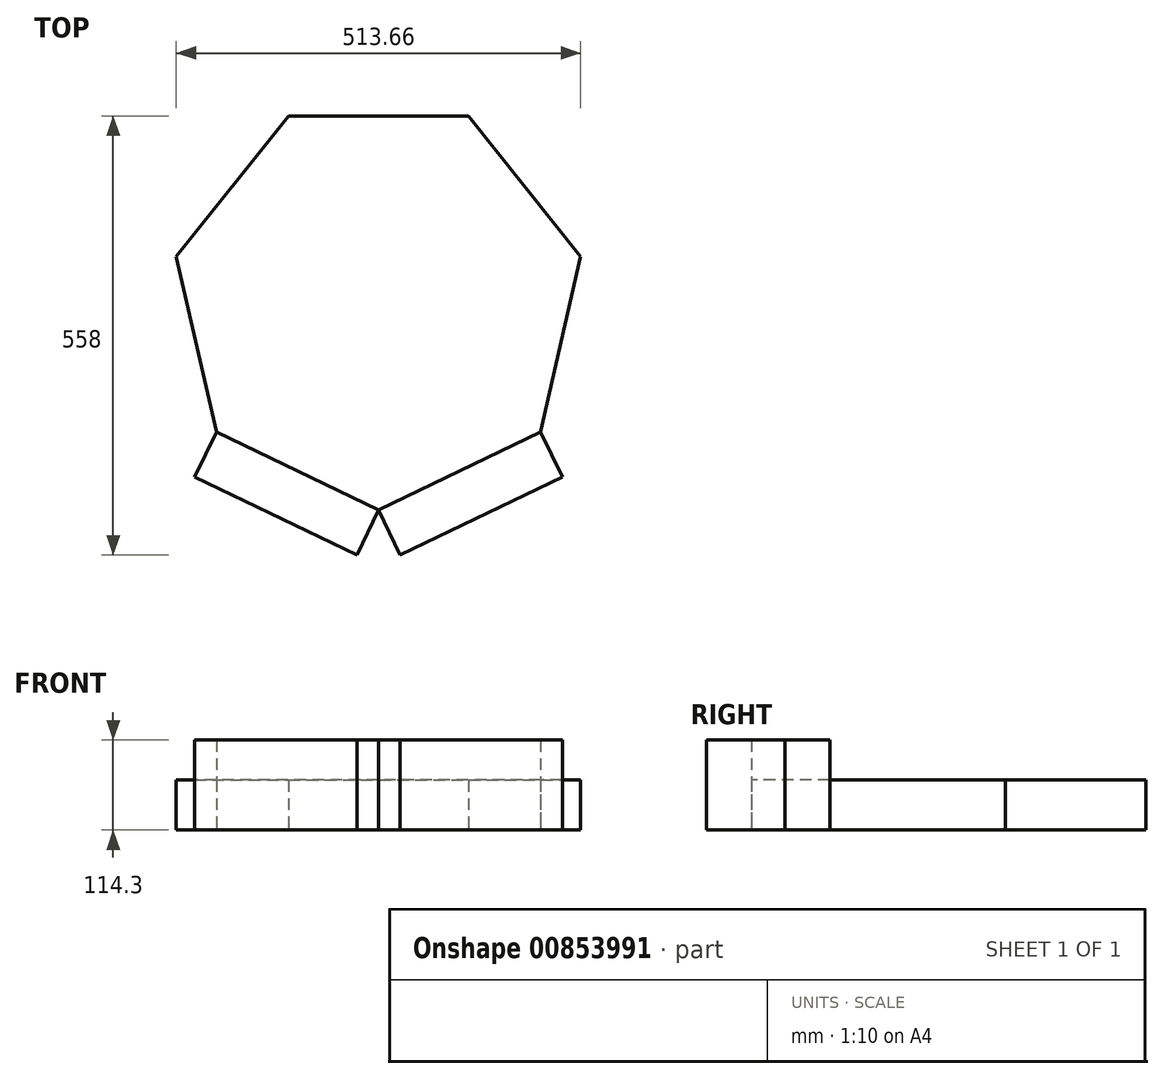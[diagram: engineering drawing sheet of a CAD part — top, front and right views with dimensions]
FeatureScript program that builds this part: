
annotation { "Feature Type Name" : "Feature", "Feature Type Description" : "" }
export const myFeature = defineFeature(function(context is Context, id is Id, definition is map)
    precondition{}
    {
        {
            var Q0;
            Q0=qCreatedBy(makeId("Top.planeOp"),FACE);
            var sketch = newSketch(context, id + "F0", { "sketchPlane" : qUnion([Q0])});
            skCircle(sketch, "E0.cCircle", {"center": v(0, 0) * mm, "radius": 237.35 * mm, "construction": true});
            skLineSegment(sketch, "E0.0", {"start": v(-114.3, 237.35) * mm, "end": v(114.3, 237.35) * mm});
            skLineSegment(sketch, "E0.1", {"start": v(114.3, 237.35) * mm, "end": v(256.83, 58.62) * mm});
            skLineSegment(sketch, "E0.2", {"start": v(256.83, 58.62) * mm, "end": v(205.96, -164.25) * mm});
            skLineSegment(sketch, "E0.3", {"start": v(205.96, -164.25) * mm, "end": v(0, -263.43) * mm});
            skLineSegment(sketch, "E0.4", {"start": v(0, -263.43) * mm, "end": v(-205.96, -164.25) * mm});
            skLineSegment(sketch, "E0.5", {"start": v(-205.96, -164.25) * mm, "end": v(-256.83, 58.62) * mm});
            skLineSegment(sketch, "E0.6", {"start": v(-256.83, 58.62) * mm, "end": v(-114.3, 237.35) * mm});
            skPoint(sketch, "E0.0.midPoint", {"position": v(0, 237.35) * mm});
            skSolve(sketch);
        }
        {
            var Q0;
            Q0 = qSketchRegion(id + "F0", true);
            extrude(context, id + "F1", {"entities" : qUnion([Q0]), "depth" : 63.5 * mm, "offsetDistance" : 25.4 * mm});
        }
        {
            var Q0;
            Q0=makeQuery(id+"F1.opExtrude","SWEPT_FACE",FACE,{"disambiguationData":[OSD([sQuery(id+"F0.wireOp",EDGE,"E0.4")])]});
            var sketch = newSketch(context, id + "F2", { "sketchPlane" : qUnion([Q0])});
            skLineSegment(sketch, "E1.bottom", {"start": v(-114.3, 0) * mm, "end": v(114.3, 0) * mm});
            skLineSegment(sketch, "E1.top", {"start": v(-114.3, 114.3) * mm, "end": v(114.3, 114.3) * mm});
            skLineSegment(sketch, "E1.left", {"start": v(-114.3, 0) * mm, "end": v(-114.3, 114.3) * mm});
            skLineSegment(sketch, "E1.right", {"start": v(114.3, 0) * mm, "end": v(114.3, 114.3) * mm});
            skSolve(sketch);
        }
        {
            var Q0;
            Q0 = qSketchRegion(id + "F2", true);
            extrude(context, id + "F3", {"entities" : qUnion([Q0]), "operationType" : NewBodyOperationType.ADD, "depth" : 63.5 * mm, "offsetDistance" : 25.4 * mm});
        }
        {
            var Q0;
            Q0=makeQuery(id+"F1.opExtrude","SWEPT_FACE",FACE,{"disambiguationData":[OSD([sQuery(id+"F0.wireOp",EDGE,"E0.3")])]});
            var sketch = newSketch(context, id + "F4", { "sketchPlane" : qUnion([Q0])});
            skLineSegment(sketch, "E2.bottom", {"start": v(114.3, 0) * mm, "end": v(-114.3, 0) * mm});
            skLineSegment(sketch, "E2.top", {"start": v(114.3, 114.3) * mm, "end": v(-114.3, 114.3) * mm});
            skLineSegment(sketch, "E2.left", {"start": v(114.3, 0) * mm, "end": v(114.3, 114.3) * mm});
            skLineSegment(sketch, "E2.right", {"start": v(-114.3, 0) * mm, "end": v(-114.3, 114.3) * mm});
            skSolve(sketch);
        }
        {
            var Q0;
            Q0 = qSketchRegion(id + "F4", true);
            extrude(context, id + "F5", {"entities" : qUnion([Q0]), "depth" : 63.5 * mm, "offsetDistance" : 25.4 * mm});
        }
    });
